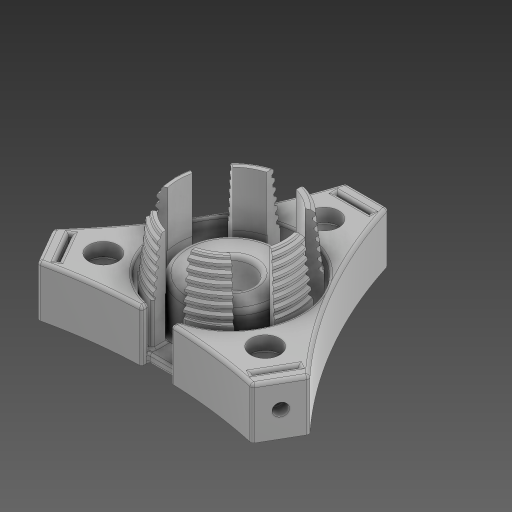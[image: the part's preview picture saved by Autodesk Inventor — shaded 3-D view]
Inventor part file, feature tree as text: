
AUTODESK INVENTOR PART (.ipt)
format: ipt  version: 2024 (Build 280153000, 153)  size: 1,858,048 bytes
history: native  units: mm
features: sketch x17, extrude x12, fillet x8, chamfer x3, hole x3, pattern_circular x3, helix x2, plane x2, projected_geometry x2, draft x1
ambient origin geometry x8: Origin, YZ Plane, XZ Plane, XY Plane, X Axis, Y Axis, Z Axis, Center Point
bodies: Solid1 (feature_tree)
feature tree (53):
  extrude  "Extrusion1"  Depth=29.5mm
  draft  "FaceDraft1"
  sketch  "Sketch2"  dims[d7=6.806784mm d8=0.55605mm]
  helix  "Coil1"  [1 undecoded]
  helix  "Coil2"  [1 undecoded]
  extrude  "Extrusion2"  Depth=0.55605mm
  extrude  "Extrusion3"  TaperAngle=0.0deg  [1 undecoded]
  fillet  "Fillet1"  [1 undecoded]
  chamfer  "Chamfer1"  Distance=0.3mm Angle=45.0deg
  plane  "Work Plane1"
  extrude  "Extrusion4"  TaperAngle=0.0deg  [1 undecoded]
  extrude  "Extrusion8"  Depth=60.0mm TaperAngle=360.0deg
  hole  "Hole2"  [1 undecoded]
  sketch  "Sketch13"  dims[d58=6.0mm d65=60.0mm d67=360.0deg]
  extrude  "Extrusion11"  Depth=10.0mm TaperAngle=0.0deg
  sketch  "Sketch18"  dims[d91=33.0mm d92=12.0mm d93=0.0mm]
  fillet  "Fillet9"  Radius=31.2mm
  extrude  "Extrusion15"  Depth=31.967mm
  hole  "Hole5"  [1 undecoded]
  pattern_circular  "Circular Pattern5"  Count=3 Angle=360.0deg
  plane  "Work Plane4"
  extrude  "Extrusion16"  TaperAngle=0.0deg  [1 undecoded]
  fillet  "Fillet14"  Radius=0.75mm
  extrude  "Extrusion17"  Depth=22.0mm
  extrude  "Extrusion19"  Depth=10.0mm TaperAngle=0.0deg
  fillet  "Fillet17"  Radius=32.8mm
  fillet  "Fillet18"  Radius=9.0mm
  extrude  "Extrusion20"  Depth=0.65mm
  fillet  "Fillet20"  Radius=0.25mm
  chamfer  "Chamfer6"  Distance=7.0mm
  pattern_circular  "Circular Pattern6"  Count=6 Angle=360.0deg
  hole  "Bearing Hole"  [1 undecoded]
  chamfer  "Chamfer7"  Distance=3.2mm
  pattern_circular  "Circular Pattern7"  [2 undecoded]
  extrude  "Extrusion21"  Depth=0.65mm
  fillet  "Fillet21"  [1 undecoded]
  fillet  "Fillet22"  Radius=0.75mm
  sketch  "Sketch1"  dims[d0=24.7mm d1=29.5mm d2=12.875mm d3=0.0mm d4=1.047198mm]
  projected_geometry  "Projected Loop1"
  sketch  "Sketch3"  dims[d9=6.806784mm]
  sketch  "Sketch4"  dims[d10=2.0mm d11=10.0mm d12=70.0mm d13=-1.047198mm d14=90.0deg d15=90.0deg d16=0.0mm d17=0.0mm d18=0.6mm]
  sketch  "Sketch5"  dims[d19=2.0mm d20=10.0mm d21=10.0mm d22=1.047198mm d23=90.0deg d24=90.0deg d25=0.0mm d26=0.0mm d27=0.0mm d28=0.0mm d29=0.0mm d30=0.0mm]
  sketch  "Sketch10"  dims[d31=0.6mm d32=0.3mm d33=2.0mm d34=45.0deg]
  sketch  "Sketch11"  dims[d36=-2.0mm d42=0.0mm d43=0.0mm]
  sketch  "Sketch21"  dims[d94=5.3mm d95=6.0mm d96=10.0mm d97=7.0mm d98=90.0deg d99=8.0mm d100=20.594885mm d122=10.0mm d123=0.0mm d124=31.2mm]
  sketch  "Sketch22"  dims[d150=1.0mm d166=31.967mm]
  sketch  "Sketch25"  dims[d167=10.0mm d168=30.0deg]
  sketch  "Sketch26"  dims[d169=7.0mm d170=0.0mm]
  sketch  "Sketch28"  dims[d171=3.0mm d172=6.0mm d173=9.779mm d174=7.62mm d175=90.0deg d176=4.5mm d177=0.0mm d179=30.0mm d180=360.0deg]
  sketch  "Sketch29"  dims[d182=16.0mm d183=0.0mm d184=0.0mm d185=0.75mm]
  sketch  "Sketch30"  dims[d188=25.0mm d189=22.0mm]
  sketch  "Sketch31"  dims[d190=31.0mm d191=10.0mm d192=0.0mm d193=32.8mm d208=9.0mm d209=0.0mm d210=1.0mm d211=0.25mm d213=7.0mm d214=60.0mm d216=360.0deg d218=8.0mm d219=3.2mm d220=0.6mm d221=0.3mm d222=0.0mm d223=0.0mm d224=0.75mm d225=0.75mm d226=2.0mm d227=45.0deg d228=30.0mm d229=360.0deg d231=6.0mm d232=6.804mm d233=6.0mm d234=9.829mm d235=8.89mm d236=90.0deg d237=8.0mm d238=20.594885mm d239=22.0mm d240=17.5mm d241=1.5mm d242=2.0mm d243=45.0deg d244=30.0mm d245=360.0deg d248=2.0mm d249=13.962634mm d250=7.0mm d251=0.0mm d252=0.5mm d253=0.65mm d151=0.872665mm d152=0.5mm d153=0.872665mm d164=0.0mm d165=0.0mm]
  projected_geometry  "Project Cut Edges3"
note: 12 required parameter values undecoded (feature->parameter linkage not recoverable at this tier; creation-order binding heuristic only, values carry confidence <= 0.55)
